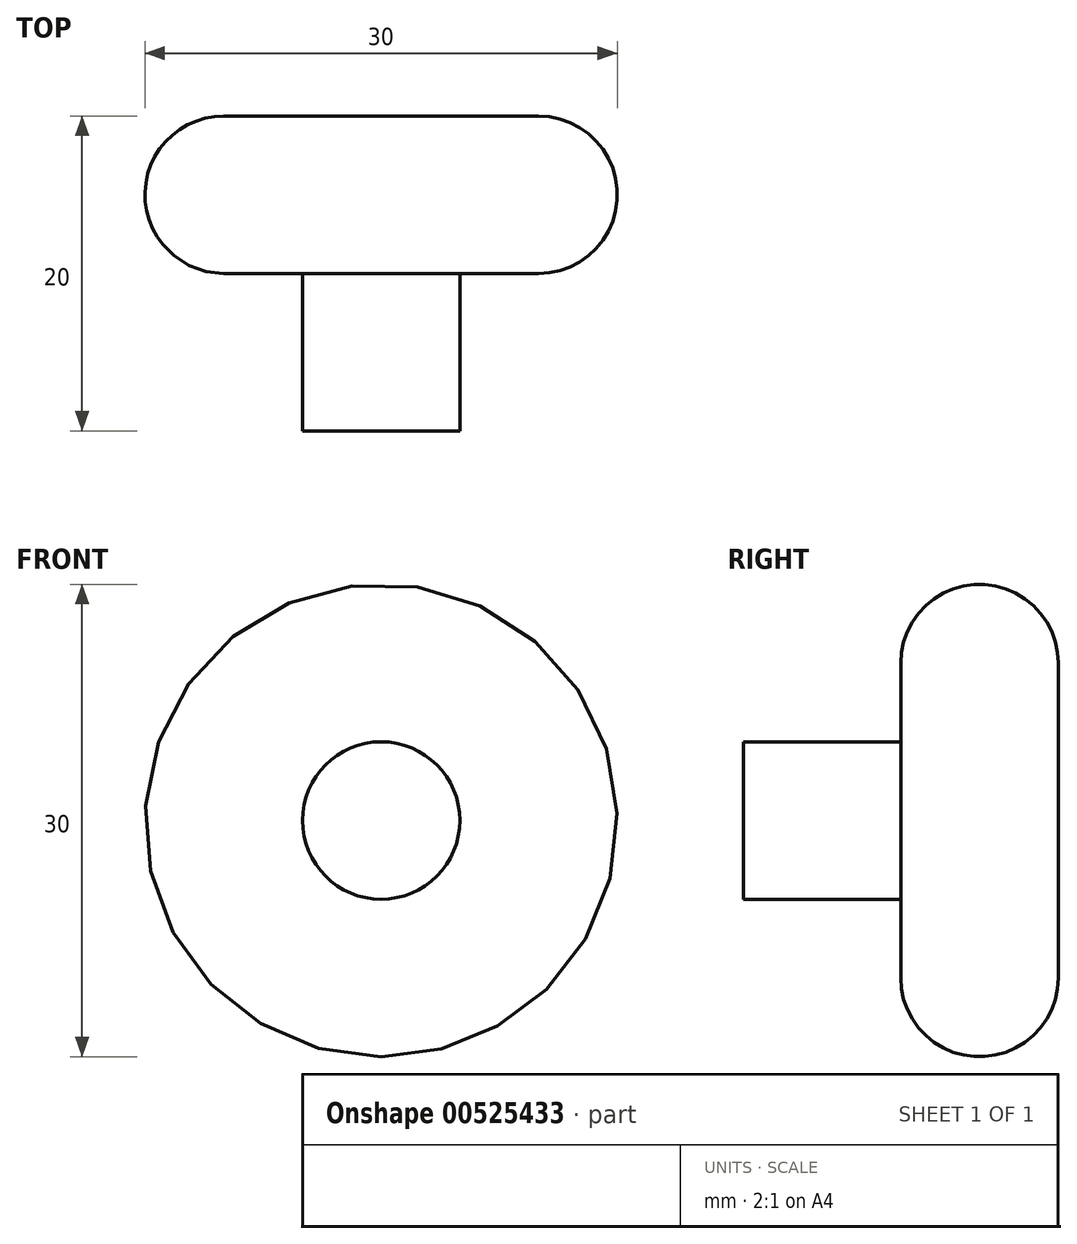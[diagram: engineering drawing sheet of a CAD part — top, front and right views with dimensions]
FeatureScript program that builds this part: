
annotation { "Feature Type Name" : "Feature", "Feature Type Description" : "" }
export const myFeature = defineFeature(function(context is Context, id is Id, definition is map)
    precondition{}
    {
        {
            var Q0;
            Q0=qCreatedBy(makeId("Front.planeOp"),FACE);
            var sketch = newSketch(context, id + "F0", { "sketchPlane" : qUnion([Q0])});
            skCircle(sketch, "E0", {"center": v(0, 0) * mm, "radius": 15 * mm});
            skSolve(sketch);
        }
        {
            var Q0;
            Q0 = qSketchRegion(id + "F0", true);
            extrude(context, id + "F1", {"entities" : qUnion([Q0]), "oppositeDirection" : true, "depth" : 10 * mm, "offsetDistance" : 25.4 * mm});
        }
        {
            var Q0;
            Q0=makeQuery(id+"F1.opExtrude","CAP_FACE",FACE,{"disambiguationData":[OSD([sQuery(id+"F0.wireOp",EDGE,"E0")])],"isStart":true});
            var sketch = newSketch(context, id + "F2", { "sketchPlane" : qUnion([Q0])});
            skCircle(sketch, "E1", {"center": v(0, 0) * mm, "radius": 5 * mm});
            skSolve(sketch);
        }
        {
            var Q0;
            Q0=makeQuery(id+"F2.imprint","IMPRINT",FACE,{"disambiguationData":[TD([[makeQuery(id+"F2.imprint","IMPRINT",EDGE,{"derivedFrom":sQuery(id+"F2.wireOp",EDGE,"E1")}),1.0]])]});
            extrude(context, id + "F3", {"entities" : qUnion([Q0]), "operationType" : NewBodyOperationType.ADD, "depth" : 10 * mm, "offsetDistance" : 25.4 * mm});
        }
        {
            var Q0;
            Q0=makeQuery(id+"F1.opExtrude","CAP_EDGE",EDGE,{"disambiguationData":[OSD([sQuery(id+"F0.wireOp",EDGE,"E0")])],"isStart":false});
            fillet(context, id + "F4", {"entities" : qUnion([Q0]), "radius" : 5 * mm, "tangentPropagation" : true, "allowEdgeOverflow" : false});
        }
        {
            var Q0;
            Q0=makeQuery(id+"F1.opExtrude","CAP_EDGE",EDGE,{"disambiguationData":[OSD([sQuery(id+"F0.wireOp",EDGE,"E0")])],"isStart":true});
            var Q1;
            Q1=makeQuery(id+"F1.opExtrude","CAP_EDGE",EDGE,{"disambiguationData":[OSD([sQuery(id+"F0.wireOp",EDGE,"E0")])],"isStart":true});
            fillet(context, id + "F5", {"entities" : qUnion([Q0, Q1]), "radius" : 5 * mm, "tangentPropagation" : true, "allowEdgeOverflow" : false});
        }
    });
